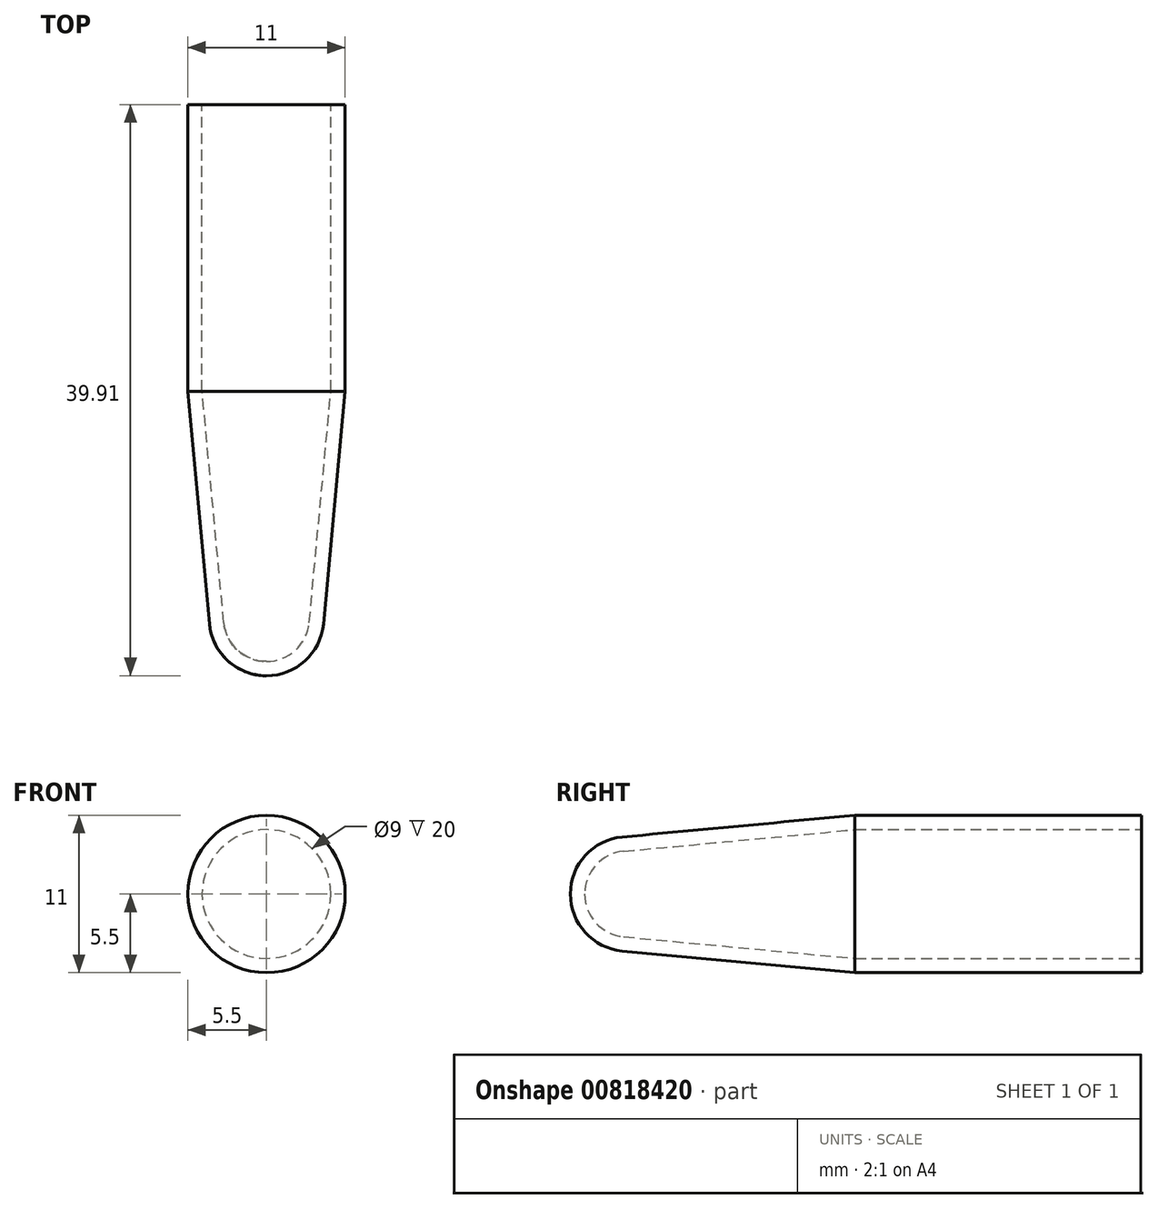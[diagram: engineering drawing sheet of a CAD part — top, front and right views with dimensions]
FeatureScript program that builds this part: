
annotation { "Feature Type Name" : "Feature", "Feature Type Description" : "" }
export const myFeature = defineFeature(function(context is Context, id is Id, definition is map)
    precondition{}
    {
        {
            var Q0;
            Q0=qCreatedBy(makeId("Front.planeOp"),FACE);
            var sketch = newSketch(context, id + "F0", { "sketchPlane" : qUnion([Q0])});
            skCircle(sketch, "E0", {"center": v(0, 0) * mm, "radius": 5 * mm});
            skSolve(sketch);
        }
        {
            var Q0;
            Q0=qCreatedBy(makeId("Top.planeOp"),FACE);
            var sketch = newSketch(context, id + "F1", { "sketchPlane" : qUnion([Q0])});
            skLineSegment(sketch, "E1.left", {"start": v(-4.5, 5) * mm, "end": v(-4.5, -15) * mm});
            skArc(sketch, "E2", {"start": v(-2.99, -31.19) * mm, "mid": v(-2.02, -33.13) * mm, "end": v(0, -33.9) * mm});
            skLineSegment(sketch, "E3", {"start": v(-4.5, -15) * mm, "end": v(-2.99, -31.19) * mm});
            skLineSegment(sketch, "E4.1", {"start": v(-5.5, -15.05) * mm, "end": v(-3.98, -31.28) * mm});
            skArc(sketch, "E4.2", {"start": v(-3.98, -31.28) * mm, "mid": v(-2.7, -33.87) * mm, "end": v(0, -34.9) * mm});
            skLineSegment(sketch, "E4.3", {"start": v(-5.5, 5) * mm, "end": v(-5.5, -15.05) * mm});
            skLineSegment(sketch, "E5", {"start": v(-4.5, 5) * mm, "end": v(-5.5, 5) * mm});
            skLineSegment(sketch, "E6", {"start": v(0, -34.9) * mm, "end": v(0, -33.9) * mm});
            skPoint(sketch, "E7.MirrorCS.end.orphan", {"position": v(2.99, -31.19) * mm});
            skPoint(sketch, "E7.MirrorCS.start.orphan", {"position": v(4.5, -15) * mm});
            skPoint(sketch, "E8.start.orphan", {"position": v(4.5, 5) * mm});
            skSolve(sketch);
        }
        {
            var Q0;
            Q0=makeQuery(id+"F1.imprint","IMPRINT",FACE,{"disambiguationData":[TD([[makeQuery(id+"F1.imprint","IMPRINT",EDGE,{"derivedFrom":sQuery(id+"F1.wireOp",EDGE,"E1.left")}),-1.0]])]});
            var Q1;
            Q1=sQuery(id+"F0.wireOp",EDGE,"E0");
            revolve(context, id + "F2", {"surfaceOperationType" : NewSurfaceOperationType.NEW, "entities" : qUnion([Q0]), "axis" : qUnion([Q1]), "revolveType" : RevolveType.FULL});
        }
    });
